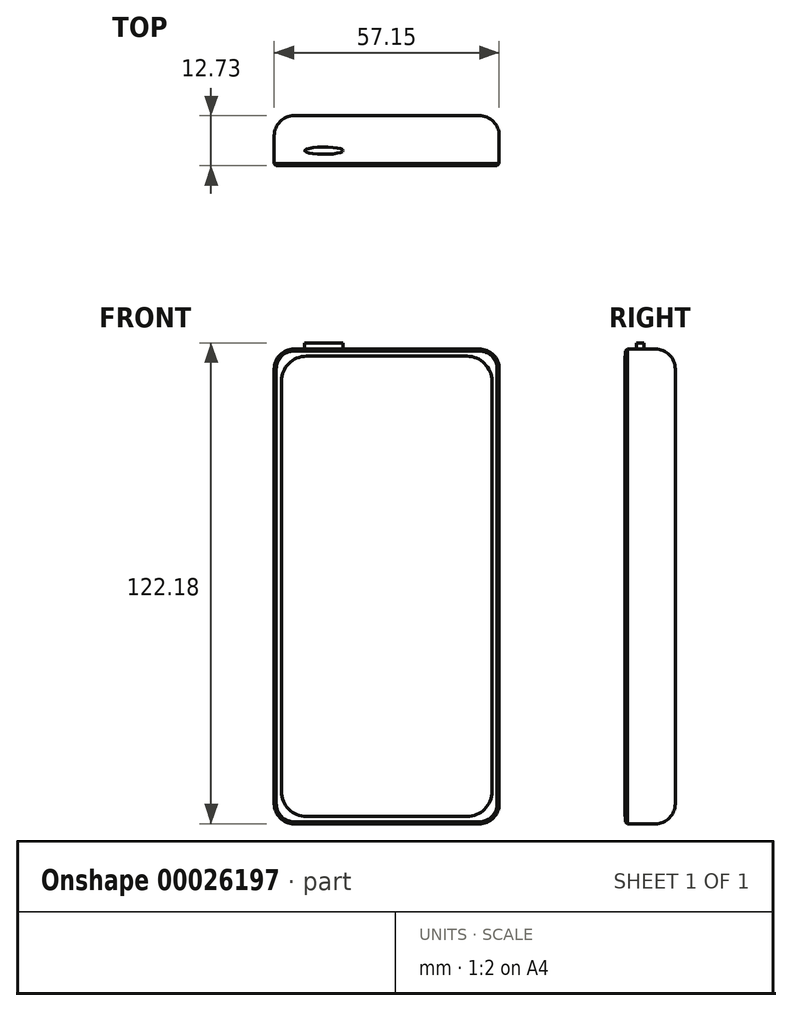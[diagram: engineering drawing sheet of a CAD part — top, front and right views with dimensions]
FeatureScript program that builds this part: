
annotation { "Feature Type Name" : "Feature", "Feature Type Description" : "" }
export const myFeature = defineFeature(function(context is Context, id is Id, definition is map)
    precondition{}
    {
        {
            var Q0;
            Q0=qCreatedBy(makeId("Front.planeOp"),FACE);
            var sketch = newSketch(context, id + "F0", { "sketchPlane" : qUnion([Q0])});
            skLineSegment(sketch, "E0.bottom", {"start": v(-28.27, 61.33) * mm, "end": v(28.88, 61.33) * mm});
            skLineSegment(sketch, "E0.top", {"start": v(-28.27, -59.32) * mm, "end": v(28.88, -59.32) * mm});
            skLineSegment(sketch, "E0.left", {"start": v(-28.27, 61.33) * mm, "end": v(-28.27, -59.32) * mm});
            skLineSegment(sketch, "E0.right", {"start": v(28.88, 61.33) * mm, "end": v(28.88, -59.32) * mm});
            skSolve(sketch);
        }
        {
            var Q0;
            Q0 = qSketchRegion(id + "F0", true);
            extrude(context, id + "F1", {"entities" : qUnion([Q0]), "depth" : 12.7 * mm});
        }
        {
            var Q0;
            Q0=makeQuery(id+"F1.opExtrude","SWEPT_EDGE",EDGE,{"disambiguationData":[OSD([sQuery(id+"F0.wireOp",EDGE,"E0.bottom"),sQuery(id+"F0.wireOp",EDGE,"E0.right")])]});
            fillet(context, id + "F2", {"entities" : qUnion([Q0]), "radius" : 5.08 * mm, "tangentPropagation" : true, "allowEdgeOverflow" : false});
        }
        {
            var Q0;
            Q0=makeQuery(id+"F1.opExtrude","CAP_EDGE",EDGE,{"disambiguationData":[OSD([sQuery(id+"F0.wireOp",EDGE,"E0.right")])],"isStart":false});
            chamfer(context, id + "F3", {"entities" : qUnion([Q0]), "width" : 0.5 * mm, "tangentPropagation" : true});
        }
        {
            var Q0;
            Q0=makeQuery(id+"F1.opExtrude","SWEPT_EDGE",EDGE,{"disambiguationData":[OSD([sQuery(id+"F0.wireOp",EDGE,"E0.bottom"),sQuery(id+"F0.wireOp",EDGE,"E0.left")])]});
            var Q1;
            Q1=makeQuery(id+"F1.opExtrude","SWEPT_EDGE",EDGE,{"disambiguationData":[OSD([sQuery(id+"F0.wireOp",EDGE,"E0.top"),sQuery(id+"F0.wireOp",EDGE,"E0.left")])]});
            var Q2;
            Q2=makeQuery(id+"F1.opExtrude","SWEPT_EDGE",EDGE,{"disambiguationData":[OSD([sQuery(id+"F0.wireOp",EDGE,"E0.top"),sQuery(id+"F0.wireOp",EDGE,"E0.right")])]});
            fillet(context, id + "F4", {"entities" : qUnion([Q0, Q1, Q2]), "radius" : 5.08 * mm, "tangentPropagation" : true, "allowEdgeOverflow" : false});
        }
        {
            var Q0;
            Q0=makeQuery(id+"F1.opExtrude","CAP_EDGE",EDGE,{"disambiguationData":[OSD([sQuery(id+"F0.wireOp",EDGE,"E0.left")])],"isStart":false});
            chamfer(context, id + "F5", {"entities" : qUnion([Q0]), "width" : 0.5 * mm, "tangentPropagation" : true});
        }
        {
            var Q0;
            Q0=makeQuery(id+"F1.opExtrude","CAP_FACE",FACE,{"disambiguationData":[OSD([sQuery(id+"F0.wireOp",EDGE,"E0.bottom"),sQuery(id+"F0.wireOp",EDGE,"E0.top"),sQuery(id+"F0.wireOp",EDGE,"E0.left"),sQuery(id+"F0.wireOp",EDGE,"E0.right")])],"isStart":true});
            fillet(context, id + "F6", {"entities" : qUnion([Q0]), "radius" : 5.08 * mm, "tangentPropagation" : true, "allowEdgeOverflow" : false});
        }
        {
            var Q0;
            Q0=makeQuery(id+"F1.opExtrude","CAP_FACE",FACE,{"disambiguationData":[OSD([sQuery(id+"F0.wireOp",EDGE,"E0.bottom"),sQuery(id+"F0.wireOp",EDGE,"E0.top"),sQuery(id+"F0.wireOp",EDGE,"E0.left"),sQuery(id+"F0.wireOp",EDGE,"E0.right")])],"isStart":false});
            var sketch = newSketch(context, id + "F7", { "sketchPlane" : qUnion([Q0])});
            skLineSegment(sketch, "E1.bottom", {"start": v(-20.07, 59.49) * mm, "end": v(20.69, 59.49) * mm});
            skLineSegment(sketch, "E1.top", {"start": v(-20.07, -57.47) * mm, "end": v(20.69, -57.47) * mm});
            skLineSegment(sketch, "E1.left", {"start": v(-26.42, 53.14) * mm, "end": v(-26.42, -51.12) * mm});
            skLineSegment(sketch, "E1.right", {"start": v(27.04, 53.14) * mm, "end": v(27.04, -51.12) * mm});
            skPoint(sketch, "E2.visualSharp", {"position": v(-26.42, 59.49) * mm});
            skArc(sketch, "E2.filletArc", {"start": v(-20.07, 59.49) * mm, "mid": v(-24.56, 57.63) * mm, "end": v(-26.42, 53.14) * mm});
            skPoint(sketch, "E3.visualSharp", {"position": v(27.04, 59.49) * mm});
            skArc(sketch, "E3.filletArc", {"start": v(27.04, 53.14) * mm, "mid": v(25.18, 57.63) * mm, "end": v(20.69, 59.49) * mm});
            skPoint(sketch, "E4.visualSharp", {"position": v(27.04, -57.47) * mm});
            skArc(sketch, "E4.filletArc", {"start": v(20.69, -57.47) * mm, "mid": v(25.18, -55.61) * mm, "end": v(27.04, -51.12) * mm});
            skPoint(sketch, "E5.visualSharp", {"position": v(-26.42, -57.47) * mm});
            skArc(sketch, "E5.filletArc", {"start": v(-26.42, -51.12) * mm, "mid": v(-24.56, -55.61) * mm, "end": v(-20.07, -57.47) * mm});
            skSolve(sketch);
        }
        {
            var Q0;
            Q0 = qSketchRegion(id + "F7", true);
            extrude(context, id + "F8", {"entities" : qUnion([Q0]), "depth" : 0.03 * mm});
        }
        {
            var Q0;
            Q0=makeQuery(id+"F1.opExtrude","SWEPT_FACE",FACE,{"disambiguationData":[OSD([sQuery(id+"F0.wireOp",EDGE,"E0.bottom")])]});
            var sketch = newSketch(context, id + "F9", { "sketchPlane" : qUnion([Q0])});
            skEllipse(sketch, "E6", {"center": v(-15.63, -8.87) * mm, "majorRadius": 4.88 * mm, "minorRadius": 0.92 * mm, "majorAxis": v(1, 0)});
            skLineSegment(sketch, "E7", {"start": v(-23.19, -8.64) * mm, "end": v(25.95, -8.64) * mm, "construction": true});
            skSolve(sketch);
        }
        {
            var Q0;
            Q0 = qSketchRegion(id + "F9", true);
            extrude(context, id + "F10", {"entities" : qUnion([Q0]), "depth" : 1.52 * mm});
        }
    });
